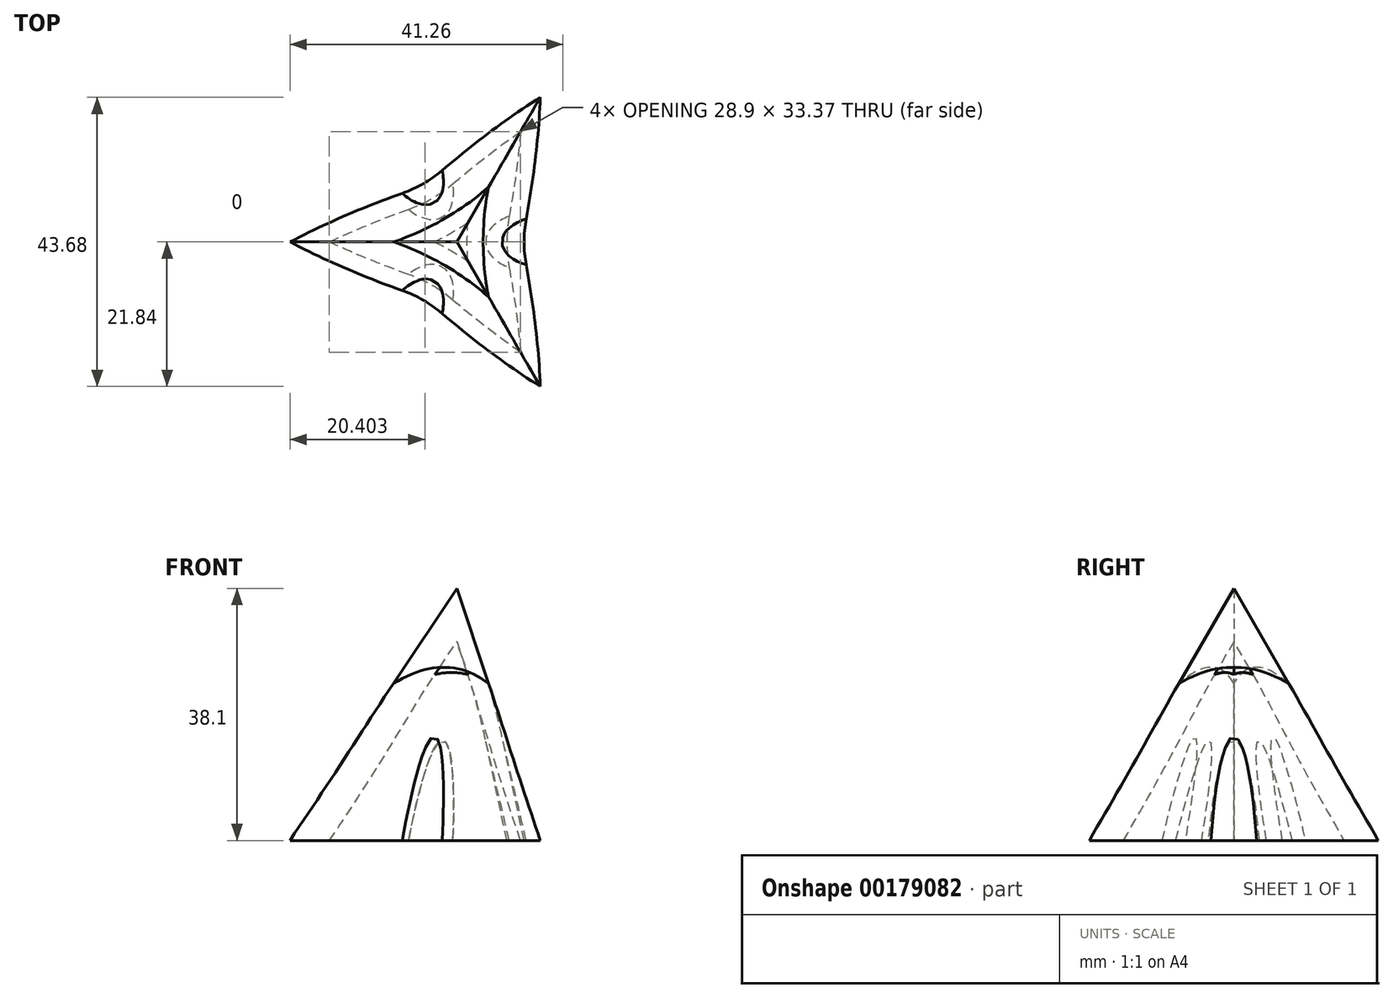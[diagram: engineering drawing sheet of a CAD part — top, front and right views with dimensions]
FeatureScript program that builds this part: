
annotation { "Feature Type Name" : "Feature", "Feature Type Description" : "" }
export const myFeature = defineFeature(function(context is Context, id is Id, definition is map)
    precondition{}
    {
        {
            var Q0;
            Q0=qCreatedBy(makeId("Top.planeOp"),FACE);
            var sketch = newSketch(context, id + "F0", { "sketchPlane" : qUnion([Q0])});
            skCircle(sketch, "E0.cCircle", {"center": v(0, 0) * mm, "radius": 12.7 * mm, "construction": true});
            skLineSegment(sketch, "E0.0", {"start": v(12.7, 22) * mm, "end": v(12.7, -22) * mm});
            skLineSegment(sketch, "E0.1", {"start": v(12.7, -22) * mm, "end": v(-25.4, 0) * mm});
            skLineSegment(sketch, "E0.2", {"start": v(-25.4, 0) * mm, "end": v(12.7, 22) * mm});
            skPoint(sketch, "E0.0.midPoint", {"position": v(12.7, 0) * mm});
            skSolve(sketch);
        }
        {
            var Q0;
            Q0=makeQuery(id+"F0.imprint","IMPRINT",FACE,{"disambiguationData":[TD([[makeQuery(id+"F0.imprint","IMPRINT",EDGE,{"derivedFrom":sQuery(id+"F0.wireOp",EDGE,"E0.0")}),-1.0]])]});
            extrude(context, id + "F1", {"entities" : qUnion([Q0]), "depth" : 38.1 * mm});
        }
        {
            var Q0;
            Q0=makeQuery(id+"F1.opExtrude","CAP_EDGE",EDGE,{"disambiguationData":[OSD([sQuery(id+"F0.wireOp",EDGE,"E0.0")])],"isStart":false});
            chamfer(context, id + "F2", {"entities" : qUnion([Q0]), "chamferType" : ChamferType.TWO_OFFSETS, "width1" : 38.1 * mm, "oppositeDirection" : false, "width2" : 12.7 * mm, "tangentPropagation" : true});
        }
        {
            var Q0;
            Q0=makeQuery(id+"F1.opExtrude","CAP_EDGE",EDGE,{"disambiguationData":[OSD([sQuery(id+"F0.wireOp",EDGE,"E0.1")])],"isStart":false});
            var Q1;
            Q1=makeQuery(id+"F1.opExtrude","CAP_EDGE",EDGE,{"disambiguationData":[OSD([sQuery(id+"F0.wireOp",EDGE,"E0.2")])],"isStart":false});
            chamfer(context, id + "F3", {"entities" : qUnion([Q0, Q1]), "chamferType" : ChamferType.TWO_OFFSETS, "width1" : 38.1 * mm, "oppositeDirection" : false, "width2" : 12.7 * mm, "tangentPropagation" : true});
        }
        {
            var Q0;
            Q0=qCreatedBy(makeId("Top.planeOp"),FACE);
            var sketch = newSketch(context, id + "F4", { "sketchPlane" : qUnion([Q0])});
            skPoint(sketch, "E1.0.midPoint", {"position": v(7.38, -12.74) * mm});
            skLineSegment(sketch, "E2", {"start": v(0, 0) * mm, "end": v(13.26, 22.97) * mm, "construction": true});
            skPoint(sketch, "E3.0.midPoint", {"position": v(7.33, 12.7) * mm});
            skCircle(sketch, "E4", {"center": v(29.21, 0) * mm, "radius": 19.05 * mm});
            skLineSegment(sketch, "E5", {"start": v(0, 0) * mm, "end": v(0, 47.42) * mm, "construction": true});
            skCircle(sketch, "E6.1.0", {"center": v(-14.6, 25.3) * mm, "radius": 19.05 * mm});
            skCircle(sketch, "E6.2.0", {"center": v(-14.6, -25.3) * mm, "radius": 19.05 * mm});
            skPoint(sketch, "E6.center", {"position": v(0, 0) * mm});
            skSolve(sketch);
        }
        {
            var Q0;
            Q0=makeQuery(id+"F4.imprint","IMPRINT",FACE,{"disambiguationData":[TD([[makeQuery(id+"F4.imprint","IMPRINT",EDGE,{"derivedFrom":sQuery(id+"F4.wireOp",EDGE,"E4")}),1.0]])]});
            var Q1;
            Q1=makeQuery(id+"F4.imprint","IMPRINT",FACE,{"disambiguationData":[TD([[makeQuery(id+"F4.imprint","IMPRINT",EDGE,{"derivedFrom":sQuery(id+"F4.wireOp",EDGE,"E6.1.0")}),1.0]])]});
            var Q2;
            Q2=makeQuery(id+"F4.imprint","IMPRINT",FACE,{"disambiguationData":[TD([[makeQuery(id+"F4.imprint","IMPRINT",EDGE,{"derivedFrom":sQuery(id+"F4.wireOp",EDGE,"E6.2.0")}),1.0]])]});
            extrude(context, id + "F5", {"entities" : qUnion([Q0, Q1, Q2]), "operationType" : NewBodyOperationType.REMOVE, "endBound" : BoundingType.THROUGH_ALL, "depth" : 25.4 * mm, "hasDraft" : true, "draftAngle" : 12 * degree, "hasSecondDirection" : true, "secondDirectionOppositeDirection" : true, "secondDirectionDepth" : 25.4 * mm});
        }
        {
            var Q0;
            Q0=makeQuery(id+"F5.boolean.opBoolean","INTERSECT",EDGE,{"derivedFrom":[makeQuery(id+"F3.opChamfer","BLEND_FACE",FACE,{"disambiguationData":[OSD([sQuery(id+"F0.wireOp",EDGE,"E0.1")])]}),makeQuery(id+"F5.split2.splitOp","SPLIT",FACE,{"derivedFrom":makeQuery(id+"F5.opExtrude","SWEPT_FACE",FACE,{"disambiguationData":[OSD([sQuery(id+"F4.wireOp",EDGE,"E6.2.0")])]})})]});
            var Q1;
            Q1=makeQuery(id+"F5.boolean.opBoolean","INTERSECT",EDGE,{"derivedFrom":[makeQuery(id+"F2.opChamfer","BLEND_FACE",FACE,{"disambiguationData":[OSD([sQuery(id+"F0.wireOp",EDGE,"E0.0")])]}),makeQuery(id+"F5.split0.splitOp","SPLIT",FACE,{"derivedFrom":makeQuery(id+"F5.opExtrude","SWEPT_FACE",FACE,{"disambiguationData":[OSD([sQuery(id+"F4.wireOp",EDGE,"E4")])]})})]});
            var Q2;
            Q2=makeQuery(id+"F5.boolean.opBoolean","INTERSECT",EDGE,{"derivedFrom":[makeQuery(id+"F3.opChamfer","BLEND_FACE",FACE,{"disambiguationData":[OSD([sQuery(id+"F0.wireOp",EDGE,"E0.2")])]}),makeQuery(id+"F5.split1.splitOp","SPLIT",FACE,{"derivedFrom":makeQuery(id+"F5.opExtrude","SWEPT_FACE",FACE,{"disambiguationData":[OSD([sQuery(id+"F4.wireOp",EDGE,"E6.1.0")])]})})]});
            fillet(context, id + "F6", {"entities" : qUnion([Q0, Q1, Q2]), "radius" : 96.53 * mm, "tangentPropagation" : true, "allowEdgeOverflow" : false});
        }
        {
            var Q0;
            Q0=makeQuery(id+"F1.opExtrude","CAP_FACE",FACE,{"disambiguationData":[OSD([sQuery(id+"F0.wireOp",EDGE,"E0.0"),sQuery(id+"F0.wireOp",EDGE,"E0.1"),sQuery(id+"F0.wireOp",EDGE,"E0.2")])],"isStart":true});
            shell(context, id + "F7", {"entities" : qUnion([Q0]), "thickness" : 2.54 * mm});
        }
    });
